# Revit family: SIMES_L.9236W_Cool Wood Bollard
name_source: partatom
category: Lighting Fixtures
revit_build: Autodesk Revit 2016 (Build: 20150714_1515(x64)
units: mm (PartAtom-declared; Revit-internal decimal feet)

## family parameters
Cut with Voids When Loaded = No
Host = Face
Light Source = Yes
OmniClass Number = 23.80.70.14
OmniClass Title = Luminaries for External Lighting
Part Type = Normal
Room Calculation Point = No
Round Connector Dimension = Use Diameter
Shared = No

## types (1)
- SIMES_L.9236W_Cool Wood Bollard
    Approval mark = CE
    Assembly Code = D5020
    Color Filter = 16777215
    Color Rendering Index = CRI 90
    Colour Temperature = 3000
    Control Gear = electronic transformer
    Default Elevation = 1219 mm
    Description = MINI-COOL BOLLARD WOOD H. 220mm
Art. L.9236W
MODULES LED 3000K  230V CRI 90 MacAdam step 3
Rated luminaire luminous flux: 488lm
Rated input power: 12.5W
Luminaire efficacy: 39lm/W
Electronic ballast 220÷240V 0/50/60Hz
CE

PRODUCT TYPE
Bollard fitting. IP rating IP 54
MATERIAL CHARACTERISTICS
Aluminium die cast housing in EN AB-47100 (low copper content) with high resistance against corrosion. Extruded EN AW-6060 aluminium structure (bollard version) with high corrosion resistance. Oiled TEAK wood finish 8mm thick. Stone wash surface treatment prior to painting process. A4 grade Stainless Steel screws with 2,5-3% molybdenum content which increases the resistance against corrosion. Silicone gaskets. Painting Process : 3 Step Process
1) Surface treatment with BONDERITE. A heavy metal free chemical surface treatment containing ceramic nano particles giving a cohesive, inorganic and highly dense protective coating. 2) PRE POLYMERIZATION a process of introducing an epoxy primer with excellent characteristics to the paint which also offers very high resistance to oxidation due to its Zinc content. 3) POLYMERIZATION a process with the application of polyester powder with high resistance against UV rays and harsh weather conditions. Resistance test protection for Marine applications for 1200h.  Mechanical resistance IK 06
LIGHTING PERFORMANCE
Toughened glass diffuser. LOR --. Colour rendering index  CRI 90, Colour stability step  MacAdam step 3. 
WIRING
Luminaire hard wired with single neoprene cable. (with cable gland Bollard versions). 
MAINTENANCE
This product has been manufactured with hand crafted procedures, therefore small imperfections, subsidence of the wood surface, actual cracks and future, colour ripples and variations over time, are deliberately present and they are a feature of the wood, proving the hand-made manufacturing procedure.  
Isolation: CLASS II . Available colours: White (cod.01), BURNISHED BRONZE (cod.20). Weight: 1.1 Kg Glow Wire test: --
Lamp included.
LOOK and COOL WOOD PATENTED
This luminaire contains built-in LED modules with energy class: A, A+, A++. In case of damage or malfunction please contact the manufacturer to receive additional instructions on how to replace and relative spare parts to order. The LED modules cannot be handled in the luminaire by the end user (Regulation UE 874/2012).
LED circuit boards are engineered accordingly to actual Lumen Maintenance regulation (LM80) and Technical Memorandum (TM21) where uniformity and quality of light is 50.000 hours referred to L70  B20 Ta 25°C.Lifecycle refers to LED circuit boards only, all others components of the luminaire are excluded.

EMERGENCY VERSIONS The fittings operates both on AC ( 50/60Hz ) and DC ( 0Hz ) voltage.
    Dimming Lamp Color Temperature Shift = <None>
    Frequency = 0/50/60Hz
    IFC Classification = Light Fixture
    IK Rating = IK 06
    Lamp = LED
    Lamp Light Flux = 1090
    Lamp count = 1
    Last Update = 02/08/2018 10:14:35
    Lifetime = 50000 L70 B20 Ta 25°C
    Light Output Ratio = 100
    Luminous efficacy = 39
    Manufacturer = SIMES
    Masterformat 2014 Code = 26 56 00
    Masterformat 2014 Description = Exterior Lighting
    Model = L.9236W
    Mounting Place = Floor
    Mounting Type = Surface mounted
    NBS Reference Code = 49
    NBS Reference Description = Luminaries And Lamps
    OmniClass Code = 23-35 47 11
    OmniClass Description = Lighting Fixture
    Photometric Web File = S7236W.ies
    Product Group = freestanding uplighter
    Product Name = Cool Wood Bollard
    Protection Class = Protection class II
    Protection Degree = IP 54
    System Light Flux = 488
    System Power = 12,5
    Tilt Angle = 90.00°
    Type Comments = SIMES S.p.A. - All rights reserved
    Type Image = cool-bollard-wood---220.jpg
    UNSPSC Code = 3911
    URL = http://www.simes.it
    Uniclass 1.4 Code = YJ73
    Uniclass 1.4 Description = Luminaries and lamps
    Uniclass 2.0 Code = PR-49
    Uniclass 2.0 Description = Luminaries and lamps
    Uniclass 2015 Code = EF_70_80
    Uniclass 2015 Name = Lighting
    Uniformat II Code = D5020
    Uniformat II Description = Lighting & Branch Wiring
    Voltage = 220÷240V
